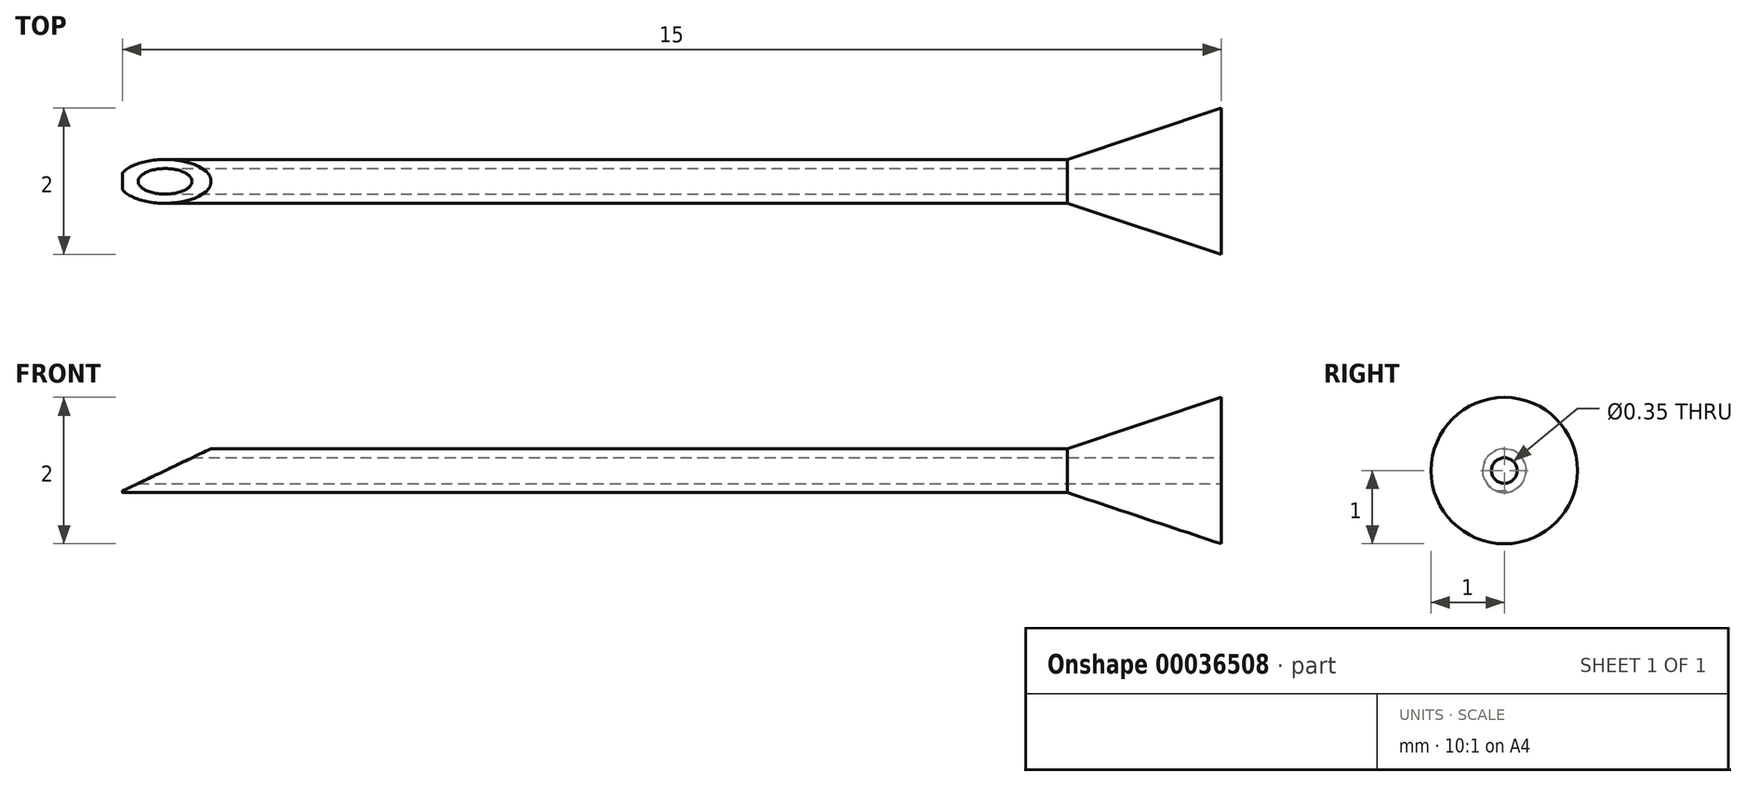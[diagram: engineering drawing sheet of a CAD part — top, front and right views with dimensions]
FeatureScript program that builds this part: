
annotation { "Feature Type Name" : "Feature", "Feature Type Description" : "" }
export const myFeature = defineFeature(function(context is Context, id is Id, definition is map)
    precondition{}
    {
        {
            var Q0;
            Q0=qCreatedBy(makeId("Front.planeOp"),FACE);
            var sketch = newSketch(context, id + "F0", { "sketchPlane" : qUnion([Q0])});
            skLineSegment(sketch, "E0", {"start": v(0, 0) * mm, "end": v(-3, 0) * mm});
            skLineSegment(sketch, "E1", {"start": v(-3, 0) * mm, "end": v(0, 1) * mm});
            skLineSegment(sketch, "E2", {"start": v(0, 1) * mm, "end": v(0, 0) * mm});
            skSolve(sketch);
        }
        {
            var Q0;
            Q0=makeQuery(id+"F0.imprint","IMPRINT",FACE,{"disambiguationData":[TD([[makeQuery(id+"F0.imprint","IMPRINT",EDGE,{"derivedFrom":sQuery(id+"F0.wireOp",EDGE,"E0")}),-1.0]])]});
            var Q1;
            Q1=sQuery(id+"F0.wireOp",EDGE,"E0");
            revolve(context, id + "F1", {"surfaceOperationType" : NewSurfaceOperationType.NEW, "entities" : qUnion([Q0]), "axis" : qUnion([Q1]), "revolveType" : RevolveType.FULL});
        }
        {
            var Q0;
            Q0=qCreatedBy(makeId("Right.planeOp"),FACE);
            var sketch = newSketch(context, id + "F2", { "sketchPlane" : qUnion([Q0])});
            skCircle(sketch, "E3", {"center": v(0, 0) * mm, "radius": 0.3 * mm});
            skSolve(sketch);
        }
        {
            var Q0;
            Q0 = qSketchRegion(id + "F2", true);
            extrude(context, id + "F3", {"entities" : qUnion([Q0]), "operationType" : NewBodyOperationType.ADD, "oppositeDirection" : true, "depth" : 15 * mm, "offsetDistance" : 25 * mm});
        }
        {
            var Q0;
            Q0=qCreatedBy(makeId("Front.planeOp"),FACE);
            var sketch = newSketch(context, id + "F4", { "sketchPlane" : qUnion([Q0])});
            skLineSegment(sketch, "E4", {"start": v(-15, -0.28) * mm, "end": v(-13.74, 0.32) * mm});
            skLineSegment(sketch, "E5", {"start": v(-13.74, 0.32) * mm, "end": v(-15.22, 0.32) * mm});
            skLineSegment(sketch, "E6", {"start": v(-15.22, 0.32) * mm, "end": v(-15, -0.28) * mm});
            skSolve(sketch);
        }
        {
            var Q0;
            Q0 = qSketchRegion(id + "F4", true);
            extrude(context, id + "F5", {"entities" : qUnion([Q0]), "operationType" : NewBodyOperationType.REMOVE, "oppositeDirection" : true, "depth" : 25 * mm, "offsetDistance" : 25 * mm});
        }
        {
            var Q0;
            Q0 = qSketchRegion(id + "F4", true);
            extrude(context, id + "F6", {"entities" : qUnion([Q0]), "operationType" : NewBodyOperationType.REMOVE, "depth" : 25 * mm, "offsetDistance" : 25 * mm});
        }
        {
            var Q0;
            Q0=makeQuery(id+"F1.opRevolve","SWEPT_FACE",FACE,{"disambiguationData":[OSD([sQuery(id+"F0.wireOp",EDGE,"E2")])]});
            var sketch = newSketch(context, id + "F7", { "sketchPlane" : qUnion([Q0])});
            skCircle(sketch, "E7", {"center": v(0, 0) * mm, "radius": 0.17 * mm});
            skSolve(sketch);
        }
        {
            var Q0;
            Q0 = qSketchRegion(id + "F7", true);
            extrude(context, id + "F8", {"entities" : qUnion([Q0]), "operationType" : NewBodyOperationType.REMOVE, "oppositeDirection" : true, "depth" : 25 * mm, "offsetDistance" : 25 * mm});
        }
    });
